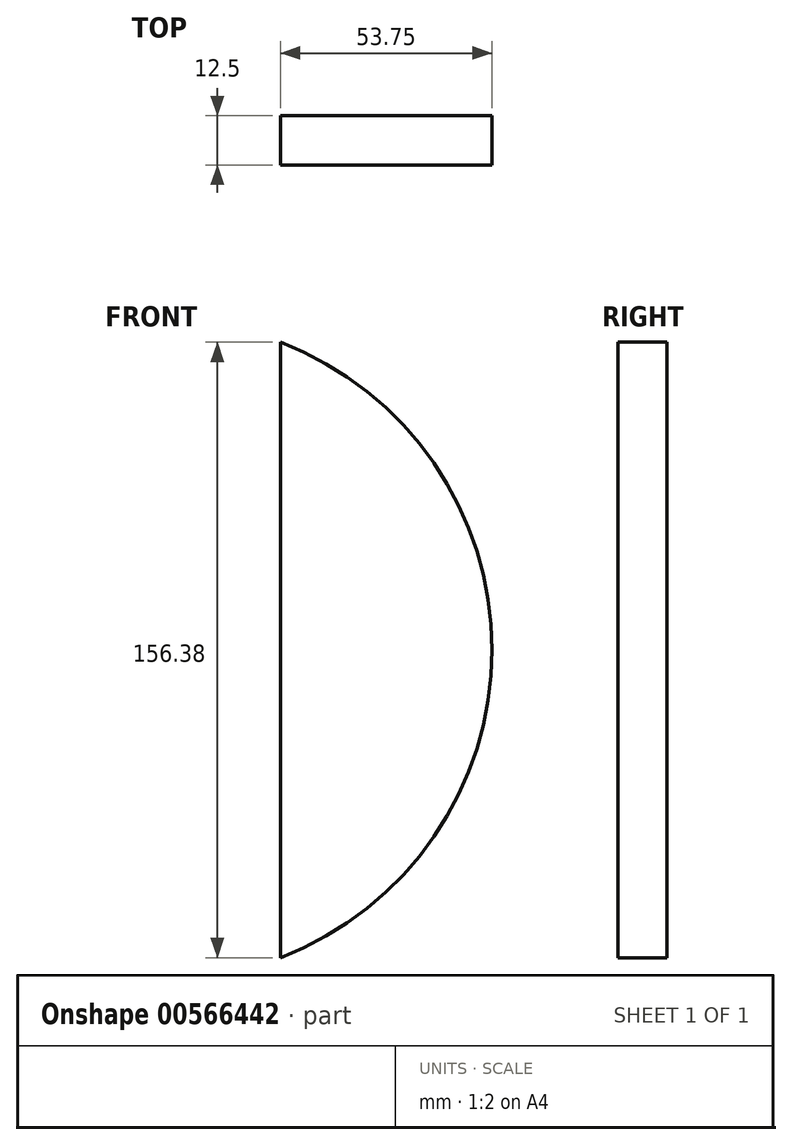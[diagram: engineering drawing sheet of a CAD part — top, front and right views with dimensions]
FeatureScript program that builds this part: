
annotation { "Feature Type Name" : "Feature", "Feature Type Description" : "" }
export const myFeature = defineFeature(function(context is Context, id is Id, definition is map)
    precondition{}
    {
        {
            var Q0;
            Q0=qCreatedBy(makeId("Front.planeOp"),FACE);
            var sketch = newSketch(context, id + "F0", { "sketchPlane" : qUnion([Q0])});
            skArc(sketch, "E0", {"start": v(0, 83.75) * mm, "mid": v(83.75, 0) * mm, "end": v(0, -83.75) * mm, "construction": true});
            skLineSegment(sketch, "E1", {"start": v(30, 78.2) * mm, "end": v(30, -78.2) * mm});
            skArc(sketch, "E2", {"start": v(30, 78.2) * mm, "mid": v(83.75, 0) * mm, "end": v(30, -78.2) * mm});
            skSolve(sketch);
        }
        {
            var Q0;
            Q0=qSketchRegion(id+"F0",true);
            extrude(context, id + "F1", {"entities" : qUnion([Q0]), "depth" : 12.5 * mm, "offsetDistance" : 25 * mm});
        }
    });
